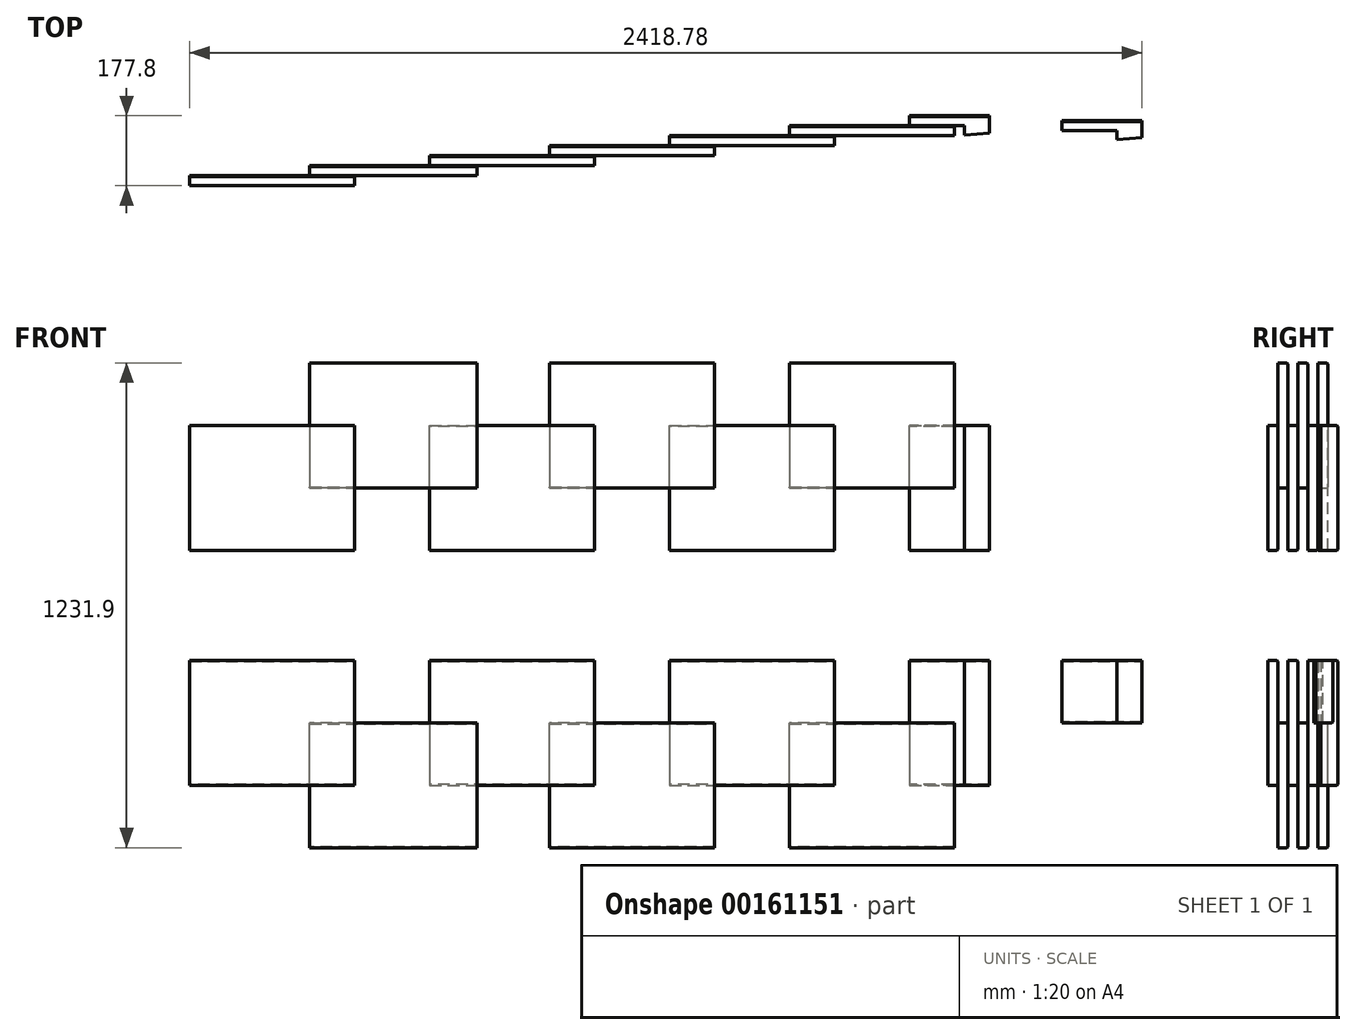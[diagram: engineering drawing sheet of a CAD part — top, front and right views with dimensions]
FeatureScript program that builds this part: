
annotation { "Feature Type Name" : "Feature", "Feature Type Description" : "" }
export const myFeature = defineFeature(function(context is Context, id is Id, definition is map)
    precondition{}
    {
        {
            var Q0;
            Q0=qCreatedBy(makeId("Top.planeOp"),FACE);
            var sketch = newSketch(context, id + "F0", { "sketchPlane" : qUnion([Q0])});
            skLineSegment(sketch, "E0.bottom", {"start": v(0, 0) * mm, "end": v(419.1, 0) * mm});
            skLineSegment(sketch, "E0.top", {"start": v(0, 25.4) * mm, "end": v(419.1, 25.4) * mm});
            skLineSegment(sketch, "E0.left", {"start": v(0, 0) * mm, "end": v(0, 25.4) * mm});
            skLineSegment(sketch, "E0.right", {"start": v(419.1, 0) * mm, "end": v(419.1, 25.4) * mm});
            skLineSegment(sketch, "E1", {"start": v(0, -217.85) * mm, "end": v(2032, -217.85) * mm});
            skLineSegment(sketch, "E2.top", {"start": v(609.6, 76.2) * mm, "end": v(1028.7, 76.2) * mm});
            skLineSegment(sketch, "E2.left", {"start": v(609.6, 50.8) * mm, "end": v(609.6, 76.2) * mm});
            skLineSegment(sketch, "E3.left", {"start": v(1028.7, 50.8) * mm, "end": v(1028.7, 76.2) * mm});
            skLineSegment(sketch, "E4.bottom", {"start": v(1219.2, 101.6) * mm, "end": v(1638.3, 101.6) * mm});
            skLineSegment(sketch, "E4.top", {"start": v(1219.2, 127) * mm, "end": v(1638.3, 127) * mm});
            skLineSegment(sketch, "E4.left", {"start": v(1219.2, 101.6) * mm, "end": v(1219.2, 127) * mm});
            skLineSegment(sketch, "E4.right", {"start": v(1638.3, 101.6) * mm, "end": v(1638.3, 127) * mm});
            skLineSegment(sketch, "E5", {"start": v(2032, 134.4) * mm, "end": v(2032, 177.8) * mm});
            skLineSegment(sketch, "E6.top", {"start": v(1828.8, 177.8) * mm, "end": v(2032, 177.8) * mm});
            skLineSegment(sketch, "E7", {"start": v(609.6, 50.8) * mm, "end": v(1028.7, 50.8) * mm});
            skLineSegment(sketch, "E8", {"start": v(1968.5, 152.4) * mm, "end": v(1828.8, 152.4) * mm});
            skLineSegment(sketch, "E9", {"start": v(1968.5, 129.12) * mm, "end": v(1968.5, 152.4) * mm});
            skLineSegment(sketch, "E10", {"start": v(1828.8, 152.4) * mm, "end": v(1828.8, 177.8) * mm});
            skLineSegment(sketch, "E11", {"start": v(0.35, -34.9) * mm, "end": v(1968.5, 129.12) * mm});
            skLineSegment(sketch, "E12.trimOffspring", {"start": v(1968.5, 129.12) * mm, "end": v(2032, 134.4) * mm});
            skSolve(sketch);
        }
        {
            var Q0;
            Q0=qSketchRegion(id+"F0",true);
            extrude(context, id + "F1", {"entities" : qUnion([Q0]), "depth" : 317.5 * mm});
        }
        {
            var Q0;
            Q0=makeQuery(id+"F1.opExtrude","CAP_EDGE",EDGE,{"disambiguationData":[OSD([sQuery(id+"F0.wireOp",EDGE,"E0.top")])],"isStart":false});
            var Q1;
            Q1=makeQuery(id+"F1.opExtrude","CAP_EDGE",EDGE,{"disambiguationData":[OSD([sQuery(id+"F0.wireOp",EDGE,"UbyaDkyD-zA3t-U79Q-e7Fc-TbQdAAhITrnT.top")])],"isStart":false});
            var Q2;
            Q2=makeQuery(id+"F1.opExtrude","CAP_EDGE",EDGE,{"disambiguationData":[OSD([sQuery(id+"F0.wireOp",EDGE,"E2.top")])],"isStart":false});
            var Q3;
            Q3=makeQuery(id+"F1.opExtrude","CAP_EDGE",EDGE,{"disambiguationData":[OSD([sQuery(id+"F0.wireOp",EDGE,"E3.top")])],"isStart":false});
            var Q4;
            Q4=makeQuery(id+"F1.opExtrude","CAP_EDGE",EDGE,{"disambiguationData":[OSD([sQuery(id+"F0.wireOp",EDGE,"E4.top")])],"isStart":false});
            var Q5;
            Q5=makeQuery(id+"F1.opExtrude","CAP_EDGE",EDGE,{"disambiguationData":[OSD([sQuery(id+"F0.wireOp",EDGE,"eHJMINtv-lgIx-npDo-GtNY-urigXcvKaI3o.top")])],"isStart":false});
            var Q6;
            Q6=makeQuery(id+"F1.opExtrude","CAP_EDGE",EDGE,{"disambiguationData":[OSD([sQuery(id+"F0.wireOp",EDGE,"E6.top")])],"isStart":false});
            var Q7;
            Q7=makeQuery(id+"F1.opExtrude","CAP_EDGE",EDGE,{"disambiguationData":[OSD([sQuery(id+"F0.wireOp",EDGE,"E6.top")])],"isStart":true});
            var Q8;
            Q8=makeQuery(id+"F1.opExtrude","CAP_EDGE",EDGE,{"disambiguationData":[OSD([sQuery(id+"F0.wireOp",EDGE,"eHJMINtv-lgIx-npDo-GtNY-urigXcvKaI3o.top")])],"isStart":true});
            var Q9;
            Q9=makeQuery(id+"F1.opExtrude","CAP_EDGE",EDGE,{"disambiguationData":[OSD([sQuery(id+"F0.wireOp",EDGE,"E4.top")])],"isStart":true});
            var Q10;
            Q10=makeQuery(id+"F1.opExtrude","CAP_EDGE",EDGE,{"disambiguationData":[OSD([sQuery(id+"F0.wireOp",EDGE,"E3.top")])],"isStart":true});
            var Q11;
            Q11=makeQuery(id+"F1.opExtrude","CAP_EDGE",EDGE,{"disambiguationData":[OSD([sQuery(id+"F0.wireOp",EDGE,"E2.top")])],"isStart":true});
            var Q12;
            Q12=makeQuery(id+"F1.opExtrude","CAP_EDGE",EDGE,{"disambiguationData":[OSD([sQuery(id+"F0.wireOp",EDGE,"UbyaDkyD-zA3t-U79Q-e7Fc-TbQdAAhITrnT.top")])],"isStart":true});
            var Q13;
            Q13=makeQuery(id+"F1.opExtrude","CAP_EDGE",EDGE,{"disambiguationData":[OSD([sQuery(id+"F0.wireOp",EDGE,"E0.top")])],"isStart":true});
            chamfer(context, id + "F2", {"entities" : qUnion([Q0, Q1, Q2, Q3, Q4, Q5, Q6, Q7, Q8, Q9, Q10, Q11, Q12, Q13]), "width" : 2.54 * mm, "tangentPropagation" : true});
        }
        {
            var Q0;
            Q0=qCreatedBy(makeId("Top.planeOp"),FACE);
            cPlane(context, id + "F3", {"entities" : qUnion([Q0]), "cplaneType" : CPlaneType.OFFSET, "offset" : 152.4 * mm, "width" : 152.4 * mm, "height" : 152.4 * mm});
        }
        {
            var Q0;
            Q0=qCreatedBy(id+"F3.planeOp",FACE);
            var sketch = newSketch(context, id + "F4", { "sketchPlane" : qUnion([Q0])});
            skLineSegment(sketch, "E13.bottom", {"start": v(304.8, 25.4) * mm, "end": v(730.08, 25.4) * mm});
            skLineSegment(sketch, "E13.top", {"start": v(304.8, 50.8) * mm, "end": v(730.08, 50.8) * mm});
            skLineSegment(sketch, "E13.left", {"start": v(304.8, 25.4) * mm, "end": v(304.8, 50.8) * mm});
            skLineSegment(sketch, "E13.right", {"start": v(730.08, 25.4) * mm, "end": v(730.08, 50.8) * mm});
            skLineSegment(sketch, "E14.bottom", {"start": v(914.4, 76.2) * mm, "end": v(1333.5, 76.2) * mm});
            skLineSegment(sketch, "E14.top", {"start": v(914.4, 101.6) * mm, "end": v(1333.5, 101.6) * mm});
            skLineSegment(sketch, "E14.left", {"start": v(914.4, 76.2) * mm, "end": v(914.4, 101.6) * mm});
            skLineSegment(sketch, "E14.right", {"start": v(1333.5, 76.2) * mm, "end": v(1333.5, 101.6) * mm});
            skLineSegment(sketch, "E15.bottom", {"start": v(1524, 127.12) * mm, "end": v(1943.1, 127.12) * mm});
            skLineSegment(sketch, "E15.top", {"start": v(1524, 152.5) * mm, "end": v(1943.1, 152.5) * mm});
            skLineSegment(sketch, "E15.left", {"start": v(1524, 127.12) * mm, "end": v(1524, 152.5) * mm});
            skLineSegment(sketch, "E15.right", {"start": v(1943.1, 127.12) * mm, "end": v(1943.1, 152.5) * mm});
            skSolve(sketch);
        }
        {
            var Q0;
            Q0=qSketchRegion(id+"F4",true);
            extrude(context, id + "F5", {"entities" : qUnion([Q0]), "oppositeDirection" : true, "depth" : 311.15 * mm, "hasSecondDirection" : true, "secondDirectionOppositeDirection" : false, "secondDirectionDepth" : 6.35 * mm});
        }
        {
            var Q0;
            Q0=makeQuery(id+"F5.opExtrude","CAP_EDGE",EDGE,{"disambiguationData":[OSD([sQuery(id+"F4.wireOp",EDGE,"E13.top")])],"isStart":true});
            var Q1;
            Q1=makeQuery(id+"F5.opExtrude","CAP_EDGE",EDGE,{"disambiguationData":[OSD([sQuery(id+"F4.wireOp",EDGE,"E13.top")])],"isStart":false});
            var Q2;
            Q2=makeQuery(id+"F5.opExtrude","CAP_EDGE",EDGE,{"disambiguationData":[OSD([sQuery(id+"F4.wireOp",EDGE,"E14.top")])],"isStart":false});
            var Q3;
            Q3=makeQuery(id+"F5.opExtrude","CAP_EDGE",EDGE,{"disambiguationData":[OSD([sQuery(id+"F4.wireOp",EDGE,"E14.top")])],"isStart":true});
            var Q4;
            Q4=makeQuery(id+"F5.opExtrude","CAP_EDGE",EDGE,{"disambiguationData":[OSD([sQuery(id+"F4.wireOp",EDGE,"E15.top")])],"isStart":false});
            var Q5;
            Q5=makeQuery(id+"F5.opExtrude","CAP_EDGE",EDGE,{"disambiguationData":[OSD([sQuery(id+"F4.wireOp",EDGE,"E15.top")])],"isStart":true});
            chamfer(context, id + "F6", {"entities" : qUnion([Q0, Q1, Q2, Q3, Q4, Q5]), "width" : 2.54 * mm, "tangentPropagation" : true});
        }
        {
            var Q0;
            Q0=makeQuery(id+"F1.opExtrude","CAP_FACE",FACE,{"disambiguationData":[OSD([sQuery(id+"F0.wireOp",EDGE,"E5"),sQuery(id+"F0.wireOp",EDGE,"E6.top"),sQuery(id+"F0.wireOp",EDGE,"E8"),sQuery(id+"F0.wireOp",EDGE,"E9"),sQuery(id+"F0.wireOp",EDGE,"E10"),sQuery(id+"F0.wireOp",EDGE,"E12.trimOffspring")])],"isStart":false});
            var sketch = newSketch(context, id + "F7", { "sketchPlane" : qUnion([Q0])});
            skLineSegment(sketch, "E16", {"start": v(2215.58, 165.85) * mm, "end": v(2418.78, 165.85) * mm});
            skLineSegment(sketch, "E17", {"start": v(2418.78, 165.85) * mm, "end": v(2418.78, 122.46) * mm});
            skLineSegment(sketch, "E18", {"start": v(2355.28, 117.15) * mm, "end": v(2355.28, 140.45) * mm});
            skLineSegment(sketch, "E19", {"start": v(2355.28, 140.45) * mm, "end": v(2215.58, 140.45) * mm});
            skLineSegment(sketch, "E20", {"start": v(2355.28, 117.15) * mm, "end": v(2418.78, 122.46) * mm});
            skLineSegment(sketch, "E21", {"start": v(2215.58, 165.85) * mm, "end": v(2215.58, 140.45) * mm});
            skSolve(sketch);
        }
        {
            var Q0;
            Q0=qSketchRegion(id+"F7",true);
            extrude(context, id + "F8", {"entities" : qUnion([Q0]), "oppositeDirection" : true, "depth" : 158.75 * mm});
        }
        {
            var Q0;
            Q0=makeQuery(id+"F8.opExtrude","CAP_EDGE",EDGE,{"disambiguationData":[OSD([sQuery(id+"F7.wireOp",EDGE,"E16")])],"isStart":true});
            var Q1;
            Q1=makeQuery(id+"F8.opExtrude","CAP_EDGE",EDGE,{"disambiguationData":[OSD([sQuery(id+"F7.wireOp",EDGE,"E16")])],"isStart":false});
            chamfer(context, id + "F9", {"entities" : qUnion([Q0, Q1]), "width" : 2.54 * mm, "tangentPropagation" : true});
        }
        {
            var Q0;
            Q0=qCreatedBy(id+"F3.planeOp",FACE);
            cPlane(context, id + "F10", {"entities" : qUnion([Q0]), "cplaneType" : CPlaneType.OFFSET, "offset" : 304.8 * mm, "width" : 152.4 * mm, "height" : 152.4 * mm});
        }
        {
            var Q0;
            Q0=makeQuery(id+"F5.opExtrude","SWEPT_BODY",BODY,{"disambiguationData":[OSD([sQuery(id+"F4.wireOp",EDGE,"E15.bottom"),sQuery(id+"F4.wireOp",EDGE,"E15.top"),sQuery(id+"F4.wireOp",EDGE,"E15.left"),sQuery(id+"F4.wireOp",EDGE,"E15.right")])]});
            var Q1;
            Q1=makeQuery(id+"F5.opExtrude","SWEPT_BODY",BODY,{"disambiguationData":[OSD([sQuery(id+"F4.wireOp",EDGE,"E14.bottom"),sQuery(id+"F4.wireOp",EDGE,"E14.top"),sQuery(id+"F4.wireOp",EDGE,"E14.left"),sQuery(id+"F4.wireOp",EDGE,"E14.right")])]});
            var Q2;
            Q2=makeQuery(id+"F5.opExtrude","SWEPT_BODY",BODY,{"disambiguationData":[OSD([sQuery(id+"F4.wireOp",EDGE,"E13.bottom"),sQuery(id+"F4.wireOp",EDGE,"E13.top"),sQuery(id+"F4.wireOp",EDGE,"E13.left"),sQuery(id+"F4.wireOp",EDGE,"E13.right")])]});
            var Q3;
            Q3=makeQuery(id+"F1.opExtrude","SWEPT_BODY",BODY,{"disambiguationData":[OSD([sQuery(id+"F0.wireOp",EDGE,"E5"),sQuery(id+"F0.wireOp",EDGE,"E6.top"),sQuery(id+"F0.wireOp",EDGE,"E8"),sQuery(id+"F0.wireOp",EDGE,"E9"),sQuery(id+"F0.wireOp",EDGE,"E10"),sQuery(id+"F0.wireOp",EDGE,"E12.trimOffspring")])]});
            var Q4;
            Q4=makeQuery(id+"F1.opExtrude","SWEPT_BODY",BODY,{"disambiguationData":[OSD([sQuery(id+"F0.wireOp",EDGE,"E4.bottom"),sQuery(id+"F0.wireOp",EDGE,"E4.top"),sQuery(id+"F0.wireOp",EDGE,"E4.left"),sQuery(id+"F0.wireOp",EDGE,"E4.right")])]});
            var Q5;
            Q5=makeQuery(id+"F1.opExtrude","SWEPT_BODY",BODY,{"disambiguationData":[OSD([sQuery(id+"F0.wireOp",EDGE,"E2.top"),sQuery(id+"F0.wireOp",EDGE,"E2.left"),sQuery(id+"F0.wireOp",EDGE,"E3.left"),sQuery(id+"F0.wireOp",EDGE,"E7")])]});
            var Q6;
            Q6=makeQuery(id+"F1.opExtrude","SWEPT_BODY",BODY,{"disambiguationData":[OSD([sQuery(id+"F0.wireOp",EDGE,"E0.bottom"),sQuery(id+"F0.wireOp",EDGE,"E0.top"),sQuery(id+"F0.wireOp",EDGE,"E0.left"),sQuery(id+"F0.wireOp",EDGE,"E0.right")])]});
            var Q7;
            Q7=qCreatedBy(id+"F10.planeOp",FACE);
            mirror(context, id + "F11", {"entities" : qUnion([Q0, Q1, Q2, Q3, Q4, Q5, Q6]), "mirrorPlane" : qUnion([Q7])});
        }
    });
